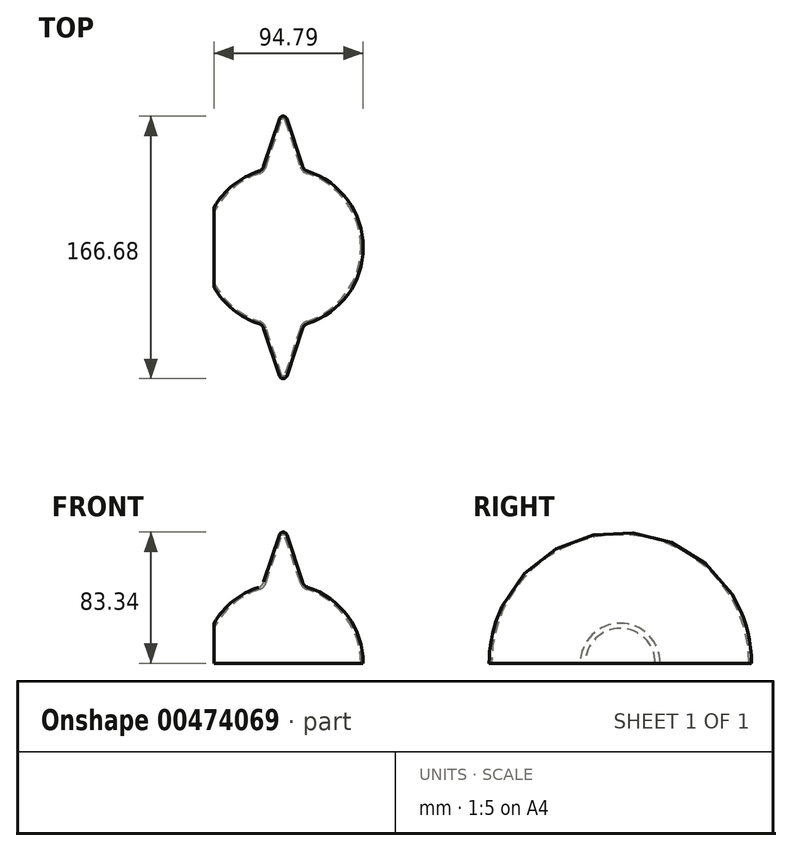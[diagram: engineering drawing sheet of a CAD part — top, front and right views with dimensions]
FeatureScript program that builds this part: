
annotation { "Feature Type Name" : "Feature", "Feature Type Description" : "" }
export const myFeature = defineFeature(function(context is Context, id is Id, definition is map)
    precondition{}
    {
        {
            var Q0;
            Q0=qCreatedBy(makeId("Top.planeOp"),FACE);
            var sketch = newSketch(context, id + "F0", { "sketchPlane" : qUnion([Q0])});
            skLineSegment(sketch, "E0", {"start": v(-77, 0) * mm, "end": v(-76.2, 0) * mm});
            skLineSegment(sketch, "E1", {"start": v(76.2, 0) * mm, "end": v(77, 0) * mm});
            skArc(sketch, "E2", {"start": v(50.8, 0) * mm, "mid": v(13.15, 49.07) * mm, "end": v(-44, 25.4) * mm});
            skLineSegment(sketch, "E3", {"start": v(-44, 0) * mm, "end": v(50.8, 0) * mm});
            skLineSegment(sketch, "E4", {"start": v(-13.15, 49.07) * mm, "end": v(0, 0) * mm, "construction": true});
            skLineSegment(sketch, "E5", {"start": v(0, 0) * mm, "end": v(13.15, 49.07) * mm, "construction": true});
            skLineSegment(sketch, "E6", {"start": v(-13.15, 49.07) * mm, "end": v(0, 88.9) * mm});
            skLineSegment(sketch, "E7", {"start": v(0, 88.9) * mm, "end": v(13.15, 49.07) * mm});
            skLineSegment(sketch, "E8", {"start": v(0, 88.9) * mm, "end": v(0, 50.8) * mm, "construction": true});
            skLineSegment(sketch, "E9", {"start": v(0, 50.8) * mm, "end": v(0, 0) * mm, "construction": true});
            skLineSegment(sketch, "E10", {"start": v(-44, 0) * mm, "end": v(-44, 25.4) * mm});
            skPoint(sketch, "E11.orphan", {"position": v(-50.8, 0) * mm});
            skSolve(sketch);
        }
        {
            var Q0;
            {var subQ0=sQuery(id+"F0.wireOp",EDGE,"E3");Q0=makeQuery(id+"F0.imprint","IMPRINT",FACE,{"disambiguationData":[TD([[makeQuery(id+"F0.imprint","IMPRINT",EDGE,{"derivedFrom":subQ0}),1.0]])]});}
            var Q1;
            {var subQ0=sQuery(id+"F0.wireOp",EDGE,"E6");Q1=makeQuery(id+"F0.imprint","IMPRINT",FACE,{"disambiguationData":[TD([[makeQuery(id+"F0.imprint","IMPRINT",EDGE,{"derivedFrom":subQ0}),-1.0]])]});}
            var Q2;
            Q2=sQuery(id+"F0.wireOp",EDGE,"E3");
            revolve(context, id + "F1", {"surfaceOperationType" : NewSurfaceOperationType.NEW, "entities" : qUnion([Q0, Q1]), "axis" : qUnion([Q2]), "revolveType" : RevolveType.ONE_DIRECTION, "angle" : 180 * degree});
        }
        {
            var Q0;
            Q0=makeQuery(id+"F1.opRevolve","SWEPT_EDGE",EDGE,{"disambiguationData":[OSD([sQuery(id+"F0.wireOp",EDGE,"E6"),sQuery(id+"F0.wireOp",EDGE,"E7")])]});
            fillet(context, id + "F2", {"entities" : qUnion([Q0]), "radius" : 2.54 * mm, "tangentPropagation" : true, "allowEdgeOverflow" : false});
        }
        {
            var Q0;
            Q0=makeQuery(id+"F1.opRevolve","SWEPT_EDGE",EDGE,{"disambiguationData":[OSD([sQuery(id+"F0.wireOp",EDGE,"E2"),sQuery(id+"F0.wireOp",EDGE,"E6")])]});
            var Q1;
            Q1=makeQuery(id+"F1.opRevolve","SWEPT_EDGE",EDGE,{"disambiguationData":[OSD([sQuery(id+"F0.wireOp",EDGE,"E2"),sQuery(id+"F0.wireOp",EDGE,"E7")])]});
            fillet(context, id + "F3", {"entities" : qUnion([Q0, Q1]), "radius" : 5.08 * mm, "tangentPropagation" : true, "allowEdgeOverflow" : false});
        }
        {
            var Q0;
            Q0=makeQuery(id+"F1.opRevolve","CAP_FACE",FACE,{"disambiguationData":[OSD([sQuery(id+"F0.wireOp",EDGE,"E2"),sQuery(id+"F0.wireOp",EDGE,"E3"),sQuery(id+"F0.wireOp",EDGE,"E6"),sQuery(id+"F0.wireOp",EDGE,"E7"),sQuery(id+"F0.wireOp",EDGE,"E10")])],"isStart":false});
            var Q1;
            Q1=makeQuery(id+"F1.opRevolve","SWEPT_FACE",FACE,{"disambiguationData":[OSD([sQuery(id+"F0.wireOp",EDGE,"E10")])]});
            shell(context, id + "F4", {"entities" : qUnion([Q0, Q1]), "thickness" : 1.5 * mm});
        }
    });
